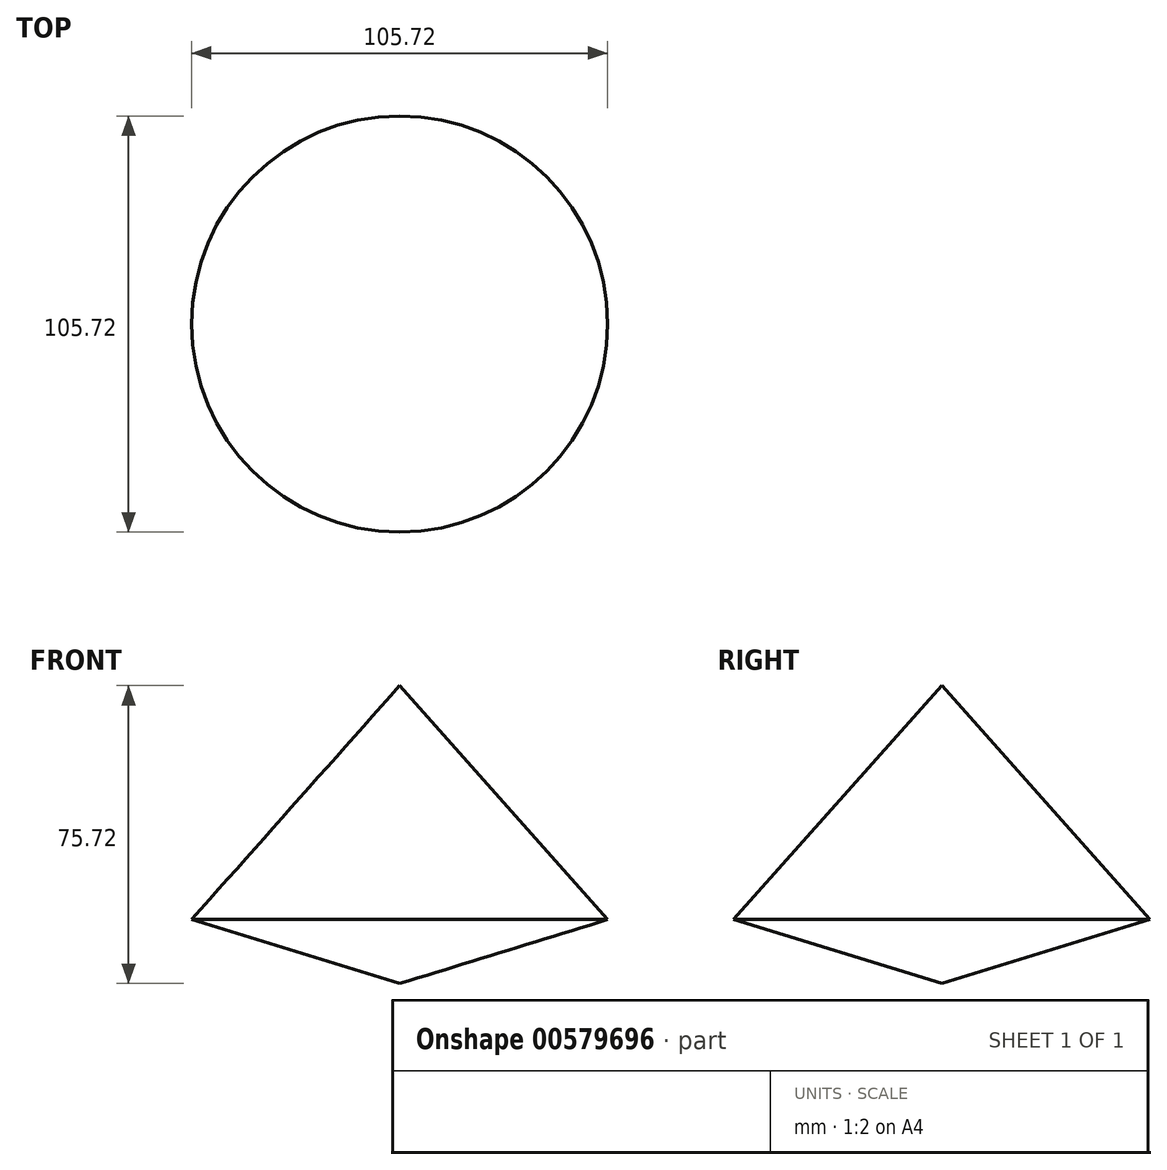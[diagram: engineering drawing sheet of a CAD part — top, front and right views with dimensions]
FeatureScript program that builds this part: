
annotation { "Feature Type Name" : "Feature", "Feature Type Description" : "" }
export const myFeature = defineFeature(function(context is Context, id is Id, definition is map)
    precondition{}
    {
        {
            var Q0;
            Q0=qCreatedBy(makeId("Front.planeOp"),FACE);
            var sketch = newSketch(context, id + "F0", { "sketchPlane" : qUnion([Q0])});
            skLineSegment(sketch, "E0", {"start": v(0, 0) * mm, "end": v(0, 75.72) * mm});
            skLineSegment(sketch, "E1", {"start": v(0, 75.72) * mm, "end": v(52.86, 16.26) * mm});
            skLineSegment(sketch, "E2", {"start": v(52.86, 16.26) * mm, "end": v(0, 0) * mm});
            skSolve(sketch);
        }
        {
            var Q0;
            Q0=makeQuery(id+"F0.imprint","IMPRINT",FACE,{"disambiguationData":[TD([[makeQuery(id+"F0.imprint","IMPRINT",EDGE,{"derivedFrom":sQuery(id+"F0.wireOp",EDGE,"E0")}),-1.0]])]});
            var Q1;
            Q1=sQuery(id+"F0.wireOp",EDGE,"E0");
            revolve(context, id + "F1", {"entities" : qUnion([Q0]), "axis" : qUnion([Q1]), "revolveType" : RevolveType.FULL});
        }
    });
